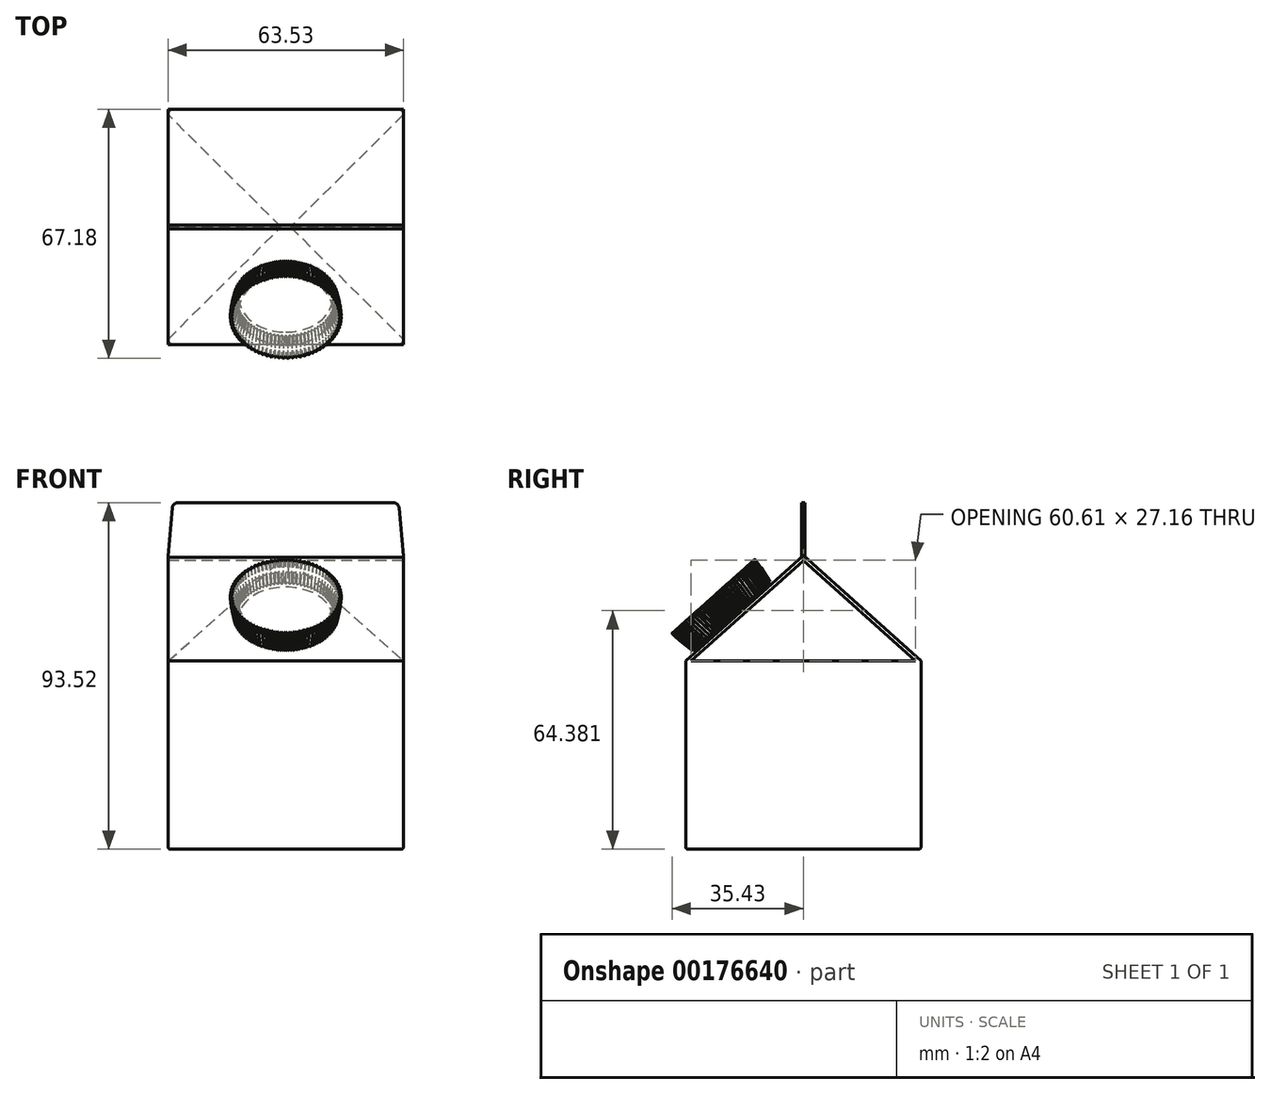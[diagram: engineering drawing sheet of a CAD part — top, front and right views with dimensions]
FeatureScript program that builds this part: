
annotation { "Feature Type Name" : "Feature", "Feature Type Description" : "" }
export const myFeature = defineFeature(function(context is Context, id is Id, definition is map)
    precondition{}
    {
        {
            var Q0;
            Q0=qCreatedBy(makeId("Top.planeOp"),FACE);
            var sketch = newSketch(context, id + "F0", { "sketchPlane" : qUnion([Q0])});
            skLineSegment(sketch, "E0.bottom", {"start": v(31.75, -31.75) * mm, "end": v(-31.75, -31.75) * mm});
            skLineSegment(sketch, "E0.top", {"start": v(31.75, 31.75) * mm, "end": v(-31.75, 31.75) * mm});
            skLineSegment(sketch, "E0.left", {"start": v(31.75, -31.75) * mm, "end": v(31.75, 31.75) * mm});
            skLineSegment(sketch, "E0.right", {"start": v(-31.75, -31.75) * mm, "end": v(-31.75, 31.75) * mm});
            skPoint(sketch, "E0.middle", {"position": v(0, 0) * mm});
            skSolve(sketch);
        }
        {
            var Q0;
            Q0=makeQuery(id+"F0.imprint","IMPRINT",FACE,{"disambiguationData":[TD([[makeQuery(id+"F0.imprint","IMPRINT",EDGE,{"derivedFrom":sQuery(id+"F0.wireOp",EDGE,"E0.bottom")}),-1.0]])]});
            extrude(context, id + "F1", {"entities" : qUnion([Q0]), "depth" : 50.8 * mm});
        }
        {
            var Q0;
            Q0=qCreatedBy(makeId("Right.planeOp"),FACE);
            var sketch = newSketch(context, id + "F2", { "sketchPlane" : qUnion([Q0])});
            skLineSegment(sketch, "E1", {"start": v(0, -61.41) * mm, "end": v(0, 100.05) * mm, "construction": true});
            skLineSegment(sketch, "E2.0", {"start": v(-31.75, 50.8) * mm, "end": v(31.75, 50.8) * mm});
            skLineSegment(sketch, "E3", {"start": v(-31.75, 50.8) * mm, "end": v(0, 79.26) * mm});
            skLineSegment(sketch, "E4", {"start": v(0, 79.26) * mm, "end": v(31.75, 50.8) * mm});
            skSolve(sketch);
        }
        {
            var Q0;
            Q0=makeQuery(id+"F2.imprint","IMPRINT",FACE,{"disambiguationData":[TD([[makeQuery(id+"F2.imprint","IMPRINT",EDGE,{"derivedFrom":sQuery(id+"F2.wireOp",EDGE,"E2.0")}),1.0]])]});
            extrude(context, id + "F3", {"entities" : qUnion([Q0]), "operationType" : NewBodyOperationType.ADD, "endBound" : BoundingType.SYMMETRIC, "depth" : 63.5 * mm});
        }
        {
            var Q0;
            Q0=makeQuery(id+"F3.boolean.opBoolean","MERGE",FACE,{"derivedFrom":[makeQuery(id+"F1.opExtrude","SWEPT_FACE",FACE,{"disambiguationData":[OSD([sQuery(id+"F0.wireOp",EDGE,"E0.right")])]}),makeQuery(id+"F3.opExtrude","CAP_FACE",FACE,{"disambiguationData":[OSD([sQuery(id+"F2.wireOp",EDGE,"E2.0"),sQuery(id+"F2.wireOp",EDGE,"E3"),sQuery(id+"F2.wireOp",EDGE,"E4")])],"isStart":true})]});
            var sketch = newSketch(context, id + "F4", { "sketchPlane" : qUnion([Q0])});
            skPoint(sketch, "E5.0", {"position": v(15.88, 65.03) * mm});
            skLineSegment(sketch, "E6.0", {"start": v(31.75, 50.8) * mm, "end": v(15.88, 65.03) * mm});
            skLineSegment(sketch, "E7.0", {"start": v(0, 77.96) * mm, "end": v(-30.3, 50.8) * mm});
            skLineSegment(sketch, "E7.1", {"start": v(30.3, 50.8) * mm, "end": v(0, 77.96) * mm});
            skLineSegment(sketch, "E8", {"start": v(-30.3, 50.8) * mm, "end": v(30.3, 50.8) * mm});
            skPoint(sketch, "E9.orphan", {"position": v(0, 79.26) * mm});
            skPoint(sketch, "E10.start.orphan", {"position": v(-31.75, 50.8) * mm});
            skSolve(sketch);
        }
        {
            var Q0;
            Q0 = qSketchRegion(id + "F4", true);
            extrude(context, id + "F5", {"entities" : qUnion([Q0]), "operationType" : NewBodyOperationType.REMOVE, "endBound" : BoundingType.THROUGH_ALL, "oppositeDirection" : true, "depth" : 25.4 * mm});
        }
        {
            var Q0;
            Q0=qCreatedBy(makeId("Front.planeOp"),FACE);
            var sketch = newSketch(context, id + "F6", { "sketchPlane" : qUnion([Q0])});
            skLineSegment(sketch, "E11.0", {"start": v(31.75, 50.8) * mm, "end": v(-31.75, 50.8) * mm});
            skLineSegment(sketch, "E12", {"start": v(0, 0) * mm, "end": v(0, 79.1) * mm, "construction": true});
            skLineSegment(sketch, "E13", {"start": v(-31.75, 50.8) * mm, "end": v(0, 79.1) * mm});
            skLineSegment(sketch, "E14", {"start": v(0, 79.1) * mm, "end": v(31.75, 50.8) * mm});
            skSolve(sketch);
        }
        {
            var Q0;
            Q0=makeQuery(id+"F6.imprint","IMPRINT",FACE,{"disambiguationData":[TD([[makeQuery(id+"F6.imprint","IMPRINT",EDGE,{"derivedFrom":sQuery(id+"F6.wireOp",EDGE,"E11.0")}),-1.0]])]});
            var Q1;
            Q1=makeQuery(id+"F5.boolean.opBoolean","COPY",FACE,{"derivedFrom":makeQuery(id+"F5.opExtrude","SWEPT_FACE",FACE,{"disambiguationData":[OSD([sQuery(id+"F4.wireOp",EDGE,"E7.1")])]})});
            var Q2;
            Q2=makeQuery(id+"F5.boolean.opBoolean","COPY",FACE,{"derivedFrom":makeQuery(id+"F5.opExtrude","SWEPT_FACE",FACE,{"disambiguationData":[OSD([sQuery(id+"F4.wireOp",EDGE,"E7.0")])]})});
            extrude(context, id + "F7", {"entities" : qUnion([Q0]), "operationType" : NewBodyOperationType.ADD, "endBound" : BoundingType.UP_TO_SURFACE, "endBoundEntityFace" : qUnion([Q1]), "depth" : 81.8 * mm, "hasSecondDirection" : true, "secondDirectionBound" : SecondDirectionBoundingType.UP_TO_SURFACE, "secondDirectionOppositeDirection" : true, "secondDirectionBoundEntityFace" : qUnion([Q2]), "secondDirectionDepth" : 25.4 * mm});
        }
        {
            var Q0;
            Q0=qCreatedBy(makeId("Front.planeOp"),FACE);
            var sketch = newSketch(context, id + "F8", { "sketchPlane" : qUnion([Q0])});
            skLineSegment(sketch, "E15.1", {"start": v(31.72, 79.2) * mm, "end": v(-31.78, 79.2) * mm});
            skLineSegment(sketch, "E16", {"start": v(-31.78, 79.2) * mm, "end": v(-30.65, 92.07) * mm});
            skLineSegment(sketch, "E17", {"start": v(-29.07, 93.52) * mm, "end": v(29.02, 93.52) * mm});
            skLineSegment(sketch, "E18", {"start": v(30.6, 92.07) * mm, "end": v(31.72, 79.2) * mm});
            skPoint(sketch, "E19.visualSharp", {"position": v(-30.52, 93.52) * mm});
            skArc(sketch, "E19.filletArc", {"start": v(-29.07, 93.52) * mm, "mid": v(-30.14, 93.1) * mm, "end": v(-30.65, 92.07) * mm});
            skPoint(sketch, "E20.visualSharp", {"position": v(30.47, 93.52) * mm});
            skArc(sketch, "E20.filletArc", {"start": v(30.6, 92.07) * mm, "mid": v(30.09, 93.1) * mm, "end": v(29.02, 93.52) * mm});
            skSolve(sketch);
        }
        {
            var Q0;
            Q0=makeQuery(id+"F8.imprint","IMPRINT",FACE,{"disambiguationData":[TD([[makeQuery(id+"F8.imprint","IMPRINT",EDGE,{"derivedFrom":sQuery(id+"F8.wireOp",EDGE,"E15.1")}),-1.0]])]});
            extrude(context, id + "F9", {"entities" : qUnion([Q0]), "operationType" : NewBodyOperationType.ADD, "endBound" : BoundingType.SYMMETRIC, "depth" : 0.97 * mm});
        }
        {
            var Q0;
            Q0=makeQuery(id+"F9.opExtrude","SWEPT_FACE",FACE,{"disambiguationData":[OSD([sQuery(id+"F8.wireOp",EDGE,"E15.1")])]});
            extrude(context, id + "F10", {"entities" : qUnion([Q0]), "operationType" : NewBodyOperationType.ADD, "depth" : 0.86 * mm});
        }
        {
            var Q0;
            Q0=makeQuery(id+"F1.opExtrude","CAP_FACE",FACE,{"disambiguationData":[OSD([sQuery(id+"F0.wireOp",EDGE,"E0.bottom"),sQuery(id+"F0.wireOp",EDGE,"E0.top"),sQuery(id+"F0.wireOp",EDGE,"E0.left"),sQuery(id+"F0.wireOp",EDGE,"E0.right")])],"isStart":true});
            fillet(context, id + "F11", {"entities" : qUnion([Q0]), "radius" : 0.64 * mm, "allowEdgeOverflow" : false});
        }
        {
            var Q0;
            Q0=makeQuery(id+"F3.opExtrude","SWEPT_FACE",FACE,{"disambiguationData":[OSD([sQuery(id+"F2.wireOp",EDGE,"E3")])]});
            var sketch = newSketch(context, id + "F12", { "sketchPlane" : qUnion([Q0])});
            skCircle(sketch, "E21", {"center": v(0, 27.48) * mm, "radius": 12.7 * mm});
            skCircle(sketch, "E22.0", {"center": v(0, 27.48) * mm, "radius": 14.3 * mm});
            skSolve(sketch);
        }
        {
            var Q0;
            Q0=makeQuery(id+"F12.imprint","IMPRINT",FACE,{"disambiguationData":[TD([[makeQuery(id+"F12.imprint","IMPRINT",EDGE,{"derivedFrom":sQuery(id+"F12.wireOp",EDGE,"E21")}),1.0]])]});
            extrude(context, id + "F13", {"entities" : qUnion([Q0]), "depth" : 5.36 * mm});
        }
        {
            var Q0;
            Q0 = qSketchRegion(id + "F12", true);
            var Q1;
            Q1=makeQuery(id+"F12.imprint","IMPRINT",FACE,{"disambiguationData":[TD([[makeQuery(id+"F12.imprint","IMPRINT",EDGE,{"derivedFrom":sQuery(id+"F12.wireOp",EDGE,"E21")}),1.0]])]});
            extrude(context, id + "F14", {"entities" : qUnion([Q0, Q1]), "depth" : 8 * mm, "hasDraft" : true, "draftAngle" : 5 * degree, "hasSecondDirection" : true, "secondDirectionOppositeDirection" : false, "secondDirectionDepth" : 0.74 * mm});
        }
        {
            var Q0;
            Q0=makeQuery(id+"F14.opExtrude","CAP_FACE",FACE,{"disambiguationData":[OSD([sQuery(id+"F12.wireOp",EDGE,"E22.0")])],"isStart":false});
            var sketch = newSketch(context, id + "F15", { "sketchPlane" : qUnion([Q0])});
            skLineSegment(sketch, "E23", {"start": v(0, 27.48) * mm, "end": v(0, 46.55) * mm, "construction": true});
            skLineSegment(sketch, "E24", {"start": v(0, 41.78) * mm, "end": v(-0.89, 43.16) * mm});
            skLineSegment(sketch, "E25", {"start": v(-0.89, 43.16) * mm, "end": v(0.89, 43.16) * mm});
            skLineSegment(sketch, "E26", {"start": v(0.89, 43.16) * mm, "end": v(0, 41.78) * mm});
            skSolve(sketch);
        }
        {
            var Q0;
            {var subQ0=sQuery(id+"F15.wireOp",EDGE,"E25");Q0=makeQuery(id+"F15.imprint","IMPRINT",FACE,{"disambiguationData":[TD([[makeQuery(id+"F15.imprint","IMPRINT",EDGE,{"derivedFrom":subQ0}),-1.0]])]});}
            var Q1;
            {var subQ0=sQuery(id+"F15.wireOp",EDGE,"E26");var subQ1=sQuery(id+"F15.wireOp",EDGE,"E24");var subQ2=makeQuery(id+"F15.imprint","INTERSECT",VERTEX,{"derivedFrom":[subQ1,subQ0]});Q1=makeQuery(id+"F15.imprint","IMPRINT",FACE,{"disambiguationData":[TD([[makeQuery(id+"F15.imprint","IMPRINT",EDGE,{"disambiguationData":[TD([[subQ2,-1.0]])],"derivedFrom":subQ1}),-1.0]])]});}
            extrude(context, id + "F16", {"entities" : qUnion([Q0, Q1]), "oppositeDirection" : true, "depth" : 7.37 * mm, "hasDraft" : true, "draftAngle" : 5 * degree});
        }
        {
            var Q0;
            Q0=makeQuery(id+"F16.opExtrude","SWEPT_BODY",BODY,{"disambiguationData":[OSD([sQuery(id+"F15.wireOp",EDGE,"E24"),sQuery(id+"F15.wireOp",EDGE,"E25"),sQuery(id+"F15.wireOp",EDGE,"E26")])]});
            var Q1;
            Q1=makeQuery(id+"F14.opExtrude","CAP_EDGE",EDGE,{"disambiguationData":[OSD([sQuery(id+"F12.wireOp",EDGE,"E22.0")])],"isStart":false});
            circularPattern(context, id + "F17", {"operationType" : NewBodyOperationType.REMOVE, "entities" : qUnion([Q0]), "axis" : qUnion([Q1]), "angle" : 360 * degree, "instanceCount" : 80, "equalSpace" : true});
        }
    });
